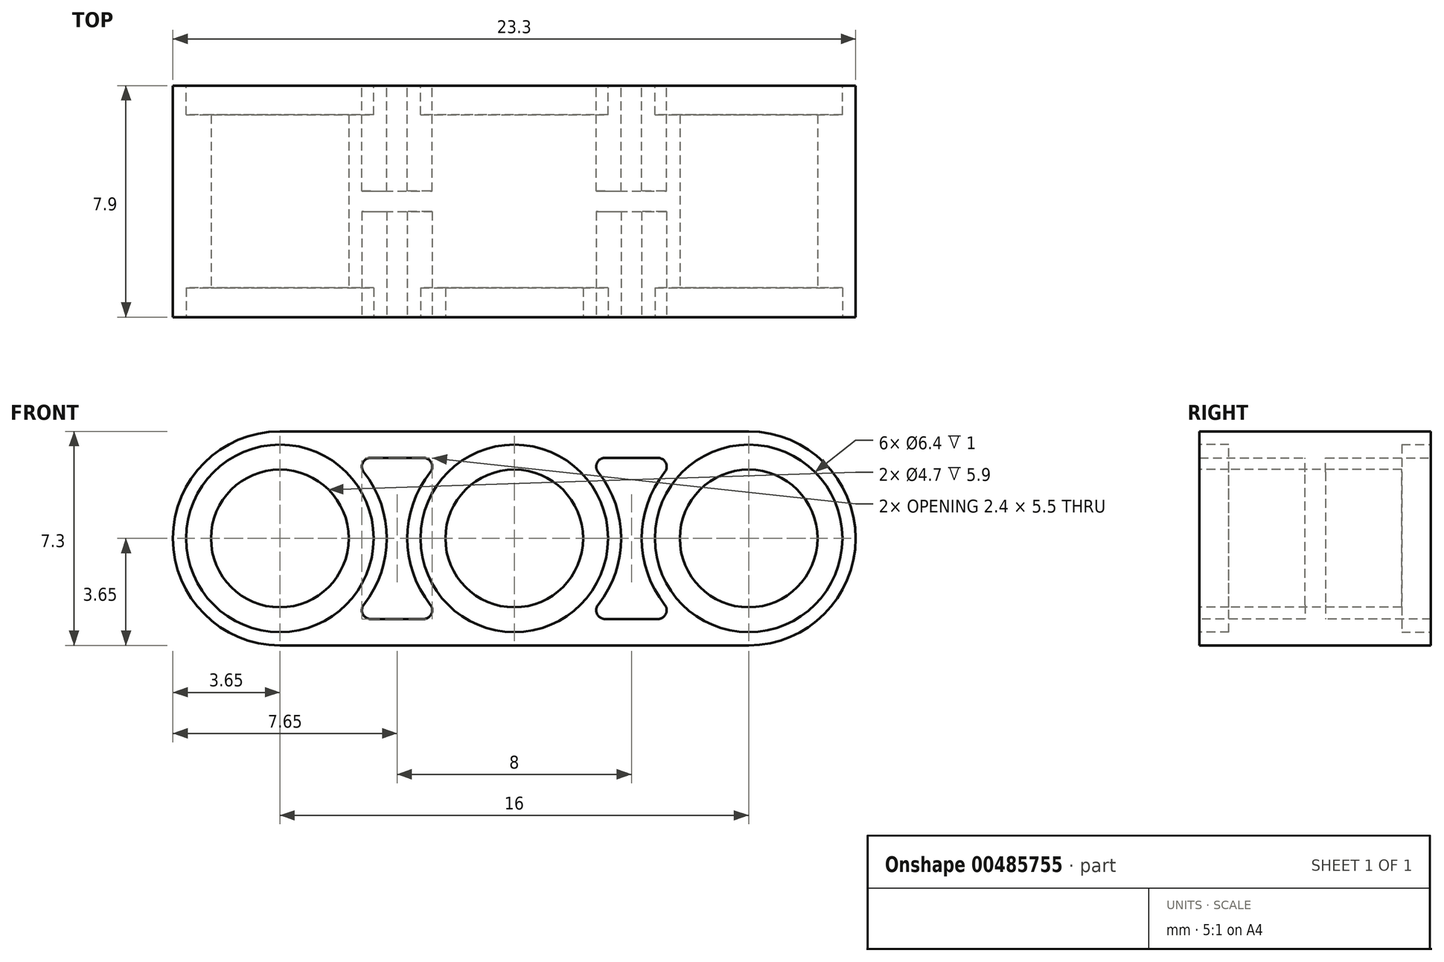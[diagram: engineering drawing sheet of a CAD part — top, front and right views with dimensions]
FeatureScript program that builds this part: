
annotation { "Feature Type Name" : "Feature", "Feature Type Description" : "" }
export const myFeature = defineFeature(function(context is Context, id is Id, definition is map)
    precondition{}
    {
        {
            var Q0;
            Q0=qCreatedBy(makeId("Front.planeOp"),FACE);
            var sketch = newSketch(context, id + "F0", { "sketchPlane" : qUnion([Q0])});
            skLineSegment(sketch, "E0.bottom", {"start": v(8, -3.65) * mm, "end": v(-8, -3.65) * mm});
            skLineSegment(sketch, "E0.top", {"start": v(8, 3.65) * mm, "end": v(-8, 3.65) * mm});
            skPoint(sketch, "E0.middle", {"position": v(0, 0) * mm});
            skArc(sketch, "E1", {"start": v(-8, 3.65) * mm, "mid": v(-11.65, 0) * mm, "end": v(-8, -3.65) * mm});
            skArc(sketch, "E2", {"start": v(8, -3.65) * mm, "mid": v(11.65, 0) * mm, "end": v(8, 3.65) * mm});
            skSolve(sketch);
        }
        {
            var Q0;
            Q0 = qSketchRegion(id + "F0", true);
            extrude(context, id + "F1", {"entities" : qUnion([Q0]), "depth" : 7.9 * mm, "offsetDistance" : 25 * mm});
        }
        {
            var Q0;
            Q0=makeQuery(id+"F1.opExtrude","CAP_FACE",FACE,{"disambiguationData":[OSD([sQuery(id+"F0.wireOp",EDGE,"E0.bottom"),sQuery(id+"F0.wireOp",EDGE,"E0.top"),sQuery(id+"F0.wireOp",EDGE,"E1"),sQuery(id+"F0.wireOp",EDGE,"E2")])],"isStart":false});
            var sketch = newSketch(context, id + "F2", { "sketchPlane" : qUnion([Q0])});
            skCircle(sketch, "E3", {"center": v(-8, 0) * mm, "radius": 3.2 * mm});
            skCircle(sketch, "E4", {"center": v(0, 0) * mm, "radius": 3.2 * mm});
            skCircle(sketch, "E5", {"center": v(8, 0) * mm, "radius": 3.2 * mm});
            skCircle(sketch, "E6", {"center": v(-8, 0) * mm, "radius": 2.35 * mm});
            skCircle(sketch, "E7", {"center": v(0, 0) * mm, "radius": 2.35 * mm});
            skCircle(sketch, "E8", {"center": v(8, 0) * mm, "radius": 2.35 * mm});
            skSolve(sketch);
        }
        {
            var Q0;
            Q0 = qSketchRegion(id + "F2", true);
            extrude(context, id + "F3", {"entities" : qUnion([Q0]), "operationType" : NewBodyOperationType.REMOVE, "oppositeDirection" : true, "depth" : 1 * mm, "offsetDistance" : 25 * mm});
        }
        {
            var Q0;
            Q0=makeQuery(id+"F3.boolean.opBoolean","SPLIT",FACE,{"disambiguationData":[TD([makeQuery(id+"F3.opExtrude","SWEPT_FACE",FACE,{"disambiguationData":[OSD([sQuery(id+"F2.wireOp",EDGE,"E7")])]})])],"derivedFrom":makeQuery(id+"F1.opExtrude","CAP_FACE",FACE,{"disambiguationData":[OSD([sQuery(id+"F0.wireOp",EDGE,"E0.bottom"),sQuery(id+"F0.wireOp",EDGE,"E0.top"),sQuery(id+"F0.wireOp",EDGE,"E1"),sQuery(id+"F0.wireOp",EDGE,"E2")])],"isStart":false})});
            var sketch = newSketch(context, id + "F4", { "sketchPlane" : qUnion([Q0])});
            skSolve(sketch);
        }
        {
            var Q0;
            Q0=makeQuery(id+"F3.boolean.opBoolean","SPLIT",FACE,{"disambiguationData":[TD([makeQuery(id+"F3.opExtrude","SWEPT_FACE",FACE,{"disambiguationData":[OSD([sQuery(id+"F2.wireOp",EDGE,"E6")])]})])],"derivedFrom":makeQuery(id+"F1.opExtrude","CAP_FACE",FACE,{"disambiguationData":[OSD([sQuery(id+"F0.wireOp",EDGE,"E0.bottom"),sQuery(id+"F0.wireOp",EDGE,"E0.top"),sQuery(id+"F0.wireOp",EDGE,"E1"),sQuery(id+"F0.wireOp",EDGE,"E2")])],"isStart":false})});
            var Q1;
            Q1 = qSketchRegion(id + "F4", true);
            var Q2;
            Q2=makeQuery(id+"F4.imprint","IMPRINT",FACE,{"disambiguationData":[TD([[makeQuery(id+"F4.imprint","IMPRINT",EDGE,{"derivedFrom":makeQuery(id+"F3.boolean.opBoolean","COPY",EDGE,{"derivedFrom":makeQuery(id+"F3.opExtrude","CAP_EDGE",EDGE,{"disambiguationData":[OSD([sQuery(id+"F2.wireOp",EDGE,"E7")])],"isStart":true})})}),1.0]])]});
            var Q3;
            Q3=makeQuery(id+"F3.boolean.opBoolean","SPLIT",FACE,{"disambiguationData":[TD([makeQuery(id+"F3.opExtrude","SWEPT_FACE",FACE,{"disambiguationData":[OSD([sQuery(id+"F2.wireOp",EDGE,"E8")])]})])],"derivedFrom":makeQuery(id+"F1.opExtrude","CAP_FACE",FACE,{"disambiguationData":[OSD([sQuery(id+"F0.wireOp",EDGE,"E0.bottom"),sQuery(id+"F0.wireOp",EDGE,"E0.top"),sQuery(id+"F0.wireOp",EDGE,"E1"),sQuery(id+"F0.wireOp",EDGE,"E2")])],"isStart":false})});
            extrude(context, id + "F5", {"entities" : qUnion([Q0, Q1, Q2, Q3]), "operationType" : NewBodyOperationType.REMOVE, "endBound" : BoundingType.THROUGH_ALL, "oppositeDirection" : true, "depth" : 25 * mm, "offsetDistance" : 25 * mm});
        }
        {
            var Q0;
            Q0=makeQuery(id+"F1.opExtrude","CAP_FACE",FACE,{"disambiguationData":[OSD([sQuery(id+"F0.wireOp",EDGE,"E0.bottom"),sQuery(id+"F0.wireOp",EDGE,"E0.top"),sQuery(id+"F0.wireOp",EDGE,"E1"),sQuery(id+"F0.wireOp",EDGE,"E2")])],"isStart":true});
            var sketch = newSketch(context, id + "F6", { "sketchPlane" : qUnion([Q0])});
            skCircle(sketch, "E9", {"center": v(8, 0) * mm, "radius": 3.2 * mm});
            skCircle(sketch, "E10", {"center": v(0, 0) * mm, "radius": 3.2 * mm});
            skCircle(sketch, "E11", {"center": v(-8, 0) * mm, "radius": 3.2 * mm});
            skSolve(sketch);
        }
        {
            var Q0;
            Q0=makeQuery(id+"F6.imprint","IMPRINT",FACE,{"disambiguationData":[TD([[makeQuery(id+"F6.imprint","IMPRINT",EDGE,{"derivedFrom":sQuery(id+"F6.wireOp",EDGE,"E9")}),1.0]])]});
            var Q1;
            Q1=makeQuery(id+"F6.imprint","IMPRINT",FACE,{"disambiguationData":[TD([[makeQuery(id+"F6.imprint","IMPRINT",EDGE,{"derivedFrom":sQuery(id+"F6.wireOp",EDGE,"E10")}),1.0]])]});
            var Q2;
            Q2=makeQuery(id+"F6.imprint","IMPRINT",FACE,{"disambiguationData":[TD([[makeQuery(id+"F6.imprint","IMPRINT",EDGE,{"derivedFrom":sQuery(id+"F6.wireOp",EDGE,"E11")}),1.0]])]});
            extrude(context, id + "F7", {"entities" : qUnion([Q0, Q1, Q2]), "operationType" : NewBodyOperationType.REMOVE, "oppositeDirection" : true, "depth" : 1 * mm, "offsetDistance" : 25 * mm});
        }
        {
            var Q0;
            {var subQ0=sQuery(id+"F0.wireOp",EDGE,"E1");var subQ1=sQuery(id+"F0.wireOp",EDGE,"E0.top");var subQ2=sQuery(id+"F0.wireOp",EDGE,"E2");var subQ3=sQuery(id+"F0.wireOp",EDGE,"E0.bottom");Q0=makeQuery(id+"F3.boolean.opBoolean","SPLIT",FACE,{"disambiguationData":[TD([makeQuery(id+"F1.opExtrude","SWEPT_FACE",FACE,{"disambiguationData":[OSD([subQ3])]})])],"derivedFrom":makeQuery(id+"F1.opExtrude","CAP_FACE",FACE,{"disambiguationData":[OSD([subQ3,subQ1,subQ0,subQ2])],"isStart":false})});}
            var sketch = newSketch(context, id + "F8", { "sketchPlane" : qUnion([Q0])});
            skCircle(sketch, "E12", {"center": v(8, 0) * mm, "radius": 3.65 * mm});
            skCircle(sketch, "E13", {"center": v(0, 0) * mm, "radius": 3.65 * mm});
            skLineSegment(sketch, "E14", {"start": v(2.4, 2.75) * mm, "end": v(5.6, 2.75) * mm});
            skLineSegment(sketch, "E15", {"start": v(2.4, -2.75) * mm, "end": v(5.6, -2.75) * mm});
            skCircle(sketch, "E16", {"center": v(-8, 0) * mm, "radius": 3.65 * mm});
            skLineSegment(sketch, "E17", {"start": v(-5.6, 2.75) * mm, "end": v(-2.4, 2.75) * mm});
            skLineSegment(sketch, "E18", {"start": v(-5.6, -2.75) * mm, "end": v(-2.4, -2.75) * mm});
            skSolve(sketch);
        }
        {
            var Q0;
            {var subQ0=sQuery(id+"F8.wireOp",EDGE,"E14");Q0=makeQuery(id+"F8.imprint","IMPRINT",FACE,{"disambiguationData":[TD([[makeQuery(id+"F8.imprint","IMPRINT",EDGE,{"derivedFrom":subQ0}),-1.0]])]});}
            var Q1;
            {var subQ0=sQuery(id+"F8.wireOp",EDGE,"E17");Q1=makeQuery(id+"F8.imprint","IMPRINT",FACE,{"disambiguationData":[TD([[makeQuery(id+"F8.imprint","IMPRINT",EDGE,{"derivedFrom":subQ0}),-1.0]])]});}
            extrude(context, id + "F9", {"entities" : qUnion([Q0, Q1]), "operationType" : NewBodyOperationType.REMOVE, "oppositeDirection" : true, "depth" : 3.6 * mm, "offsetDistance" : 25 * mm});
        }
        {
            var Q0;
            Q0=makeQuery(id+"F1.opExtrude","CAP_FACE",FACE,{"disambiguationData":[OSD([sQuery(id+"F0.wireOp",EDGE,"E0.bottom"),sQuery(id+"F0.wireOp",EDGE,"E0.top"),sQuery(id+"F0.wireOp",EDGE,"E1"),sQuery(id+"F0.wireOp",EDGE,"E2")])],"isStart":true});
            var sketch = newSketch(context, id + "F10", { "sketchPlane" : qUnion([Q0])});
            skCircle(sketch, "E19", {"center": v(8, 0) * mm, "radius": 3.65 * mm});
            skCircle(sketch, "E20", {"center": v(0, 0) * mm, "radius": 3.65 * mm});
            skCircle(sketch, "E21", {"center": v(-8, 0) * mm, "radius": 3.65 * mm});
            skLineSegment(sketch, "E22", {"start": v(5.6, -2.75) * mm, "end": v(2.4, -2.75) * mm});
            skLineSegment(sketch, "E23", {"start": v(5.6, 2.75) * mm, "end": v(2.4, 2.75) * mm});
            skLineSegment(sketch, "E24", {"start": v(-2.4, -2.75) * mm, "end": v(-5.6, -2.75) * mm});
            skLineSegment(sketch, "E25", {"start": v(-2.4, 2.75) * mm, "end": v(-5.6, 2.75) * mm});
            skSolve(sketch);
        }
        {
            var Q0;
            {var subQ0=sQuery(id+"F10.wireOp",EDGE,"E22");Q0=makeQuery(id+"F10.imprint","IMPRINT",FACE,{"disambiguationData":[TD([[makeQuery(id+"F10.imprint","IMPRINT",EDGE,{"derivedFrom":subQ0}),-1.0]])]});}
            var Q1;
            {var subQ0=sQuery(id+"F10.wireOp",EDGE,"E24");Q1=makeQuery(id+"F10.imprint","IMPRINT",FACE,{"disambiguationData":[TD([[makeQuery(id+"F10.imprint","IMPRINT",EDGE,{"derivedFrom":subQ0}),-1.0]])]});}
            extrude(context, id + "F11", {"entities" : qUnion([Q0, Q1]), "operationType" : NewBodyOperationType.REMOVE, "oppositeDirection" : true, "depth" : 3.6 * mm, "offsetDistance" : 25 * mm});
        }
        {
            var Q0;
            Q0=makeQuery(id+"F11.boolean.opBoolean","COPY",EDGE,{"derivedFrom":makeQuery(id+"F11.opExtrude","SWEPT_EDGE",EDGE,{"disambiguationData":[OSD([sQuery(id+"F10.wireOp",EDGE,"E19"),sQuery(id+"F10.wireOp",EDGE,"E23")])]})});
            var Q1;
            Q1=makeQuery(id+"F11.boolean.opBoolean","COPY",EDGE,{"derivedFrom":makeQuery(id+"F11.opExtrude","SWEPT_EDGE",EDGE,{"disambiguationData":[OSD([sQuery(id+"F10.wireOp",EDGE,"E20"),sQuery(id+"F10.wireOp",EDGE,"E25")])]})});
            var Q2;
            Q2=makeQuery(id+"F9.boolean.opBoolean","COPY",EDGE,{"derivedFrom":makeQuery(id+"F9.opExtrude","SWEPT_EDGE",EDGE,{"disambiguationData":[OSD([sQuery(id+"F8.wireOp",EDGE,"E13"),sQuery(id+"F8.wireOp",EDGE,"E14")])]})});
            var Q3;
            Q3=makeQuery(id+"F9.boolean.opBoolean","COPY",EDGE,{"derivedFrom":makeQuery(id+"F9.opExtrude","SWEPT_EDGE",EDGE,{"disambiguationData":[OSD([sQuery(id+"F8.wireOp",EDGE,"E16"),sQuery(id+"F8.wireOp",EDGE,"E17")])]})});
            var Q4;
            Q4=makeQuery(id+"F9.boolean.opBoolean","COPY",EDGE,{"derivedFrom":makeQuery(id+"F9.opExtrude","SWEPT_EDGE",EDGE,{"disambiguationData":[OSD([sQuery(id+"F8.wireOp",EDGE,"E13"),sQuery(id+"F8.wireOp",EDGE,"E17")])]})});
            var Q5;
            Q5=makeQuery(id+"F9.boolean.opBoolean","COPY",EDGE,{"derivedFrom":makeQuery(id+"F9.opExtrude","SWEPT_EDGE",EDGE,{"disambiguationData":[OSD([sQuery(id+"F8.wireOp",EDGE,"E12"),sQuery(id+"F8.wireOp",EDGE,"E14")])]})});
            var Q6;
            Q6=makeQuery(id+"F11.boolean.opBoolean","COPY",EDGE,{"derivedFrom":makeQuery(id+"F11.opExtrude","SWEPT_EDGE",EDGE,{"disambiguationData":[OSD([sQuery(id+"F10.wireOp",EDGE,"E20"),sQuery(id+"F10.wireOp",EDGE,"E23")])]})});
            var Q7;
            Q7=makeQuery(id+"F11.boolean.opBoolean","COPY",EDGE,{"derivedFrom":makeQuery(id+"F11.opExtrude","SWEPT_EDGE",EDGE,{"disambiguationData":[OSD([sQuery(id+"F10.wireOp",EDGE,"E21"),sQuery(id+"F10.wireOp",EDGE,"E25")])]})});
            var Q8;
            Q8=makeQuery(id+"F11.boolean.opBoolean","COPY",EDGE,{"derivedFrom":makeQuery(id+"F11.opExtrude","SWEPT_EDGE",EDGE,{"disambiguationData":[OSD([sQuery(id+"F10.wireOp",EDGE,"E19"),sQuery(id+"F10.wireOp",EDGE,"E22")])]})});
            var Q9;
            Q9=makeQuery(id+"F11.boolean.opBoolean","COPY",EDGE,{"derivedFrom":makeQuery(id+"F11.opExtrude","SWEPT_EDGE",EDGE,{"disambiguationData":[OSD([sQuery(id+"F10.wireOp",EDGE,"E20"),sQuery(id+"F10.wireOp",EDGE,"E24")])]})});
            var Q10;
            Q10=makeQuery(id+"F11.boolean.opBoolean","COPY",EDGE,{"derivedFrom":makeQuery(id+"F11.opExtrude","SWEPT_EDGE",EDGE,{"disambiguationData":[OSD([sQuery(id+"F10.wireOp",EDGE,"E20"),sQuery(id+"F10.wireOp",EDGE,"E22")])]})});
            var Q11;
            Q11=makeQuery(id+"F11.boolean.opBoolean","COPY",EDGE,{"derivedFrom":makeQuery(id+"F11.opExtrude","SWEPT_EDGE",EDGE,{"disambiguationData":[OSD([sQuery(id+"F10.wireOp",EDGE,"E21"),sQuery(id+"F10.wireOp",EDGE,"E24")])]})});
            var Q12;
            Q12=makeQuery(id+"F9.boolean.opBoolean","COPY",EDGE,{"derivedFrom":makeQuery(id+"F9.opExtrude","SWEPT_EDGE",EDGE,{"disambiguationData":[OSD([sQuery(id+"F8.wireOp",EDGE,"E13"),sQuery(id+"F8.wireOp",EDGE,"E18")])]})});
            var Q13;
            Q13=makeQuery(id+"F9.boolean.opBoolean","COPY",EDGE,{"derivedFrom":makeQuery(id+"F9.opExtrude","SWEPT_EDGE",EDGE,{"disambiguationData":[OSD([sQuery(id+"F8.wireOp",EDGE,"E12"),sQuery(id+"F8.wireOp",EDGE,"E15")])]})});
            var Q14;
            Q14=makeQuery(id+"F9.boolean.opBoolean","COPY",EDGE,{"derivedFrom":makeQuery(id+"F9.opExtrude","SWEPT_EDGE",EDGE,{"disambiguationData":[OSD([sQuery(id+"F8.wireOp",EDGE,"E16"),sQuery(id+"F8.wireOp",EDGE,"E18")])]})});
            var Q15;
            Q15=makeQuery(id+"F9.boolean.opBoolean","COPY",EDGE,{"derivedFrom":makeQuery(id+"F9.opExtrude","SWEPT_EDGE",EDGE,{"disambiguationData":[OSD([sQuery(id+"F8.wireOp",EDGE,"E13"),sQuery(id+"F8.wireOp",EDGE,"E15")])]})});
            fillet(context, id + "F12", {"entities" : qUnion([Q0, Q1, Q2, Q3, Q4, Q5, Q6, Q7, Q8, Q9, Q10, Q11, Q12, Q13, Q14, Q15]), "radius" : 0.3 * mm, "tangentPropagation" : true, "allowEdgeOverflow" : false});
        }
    });
